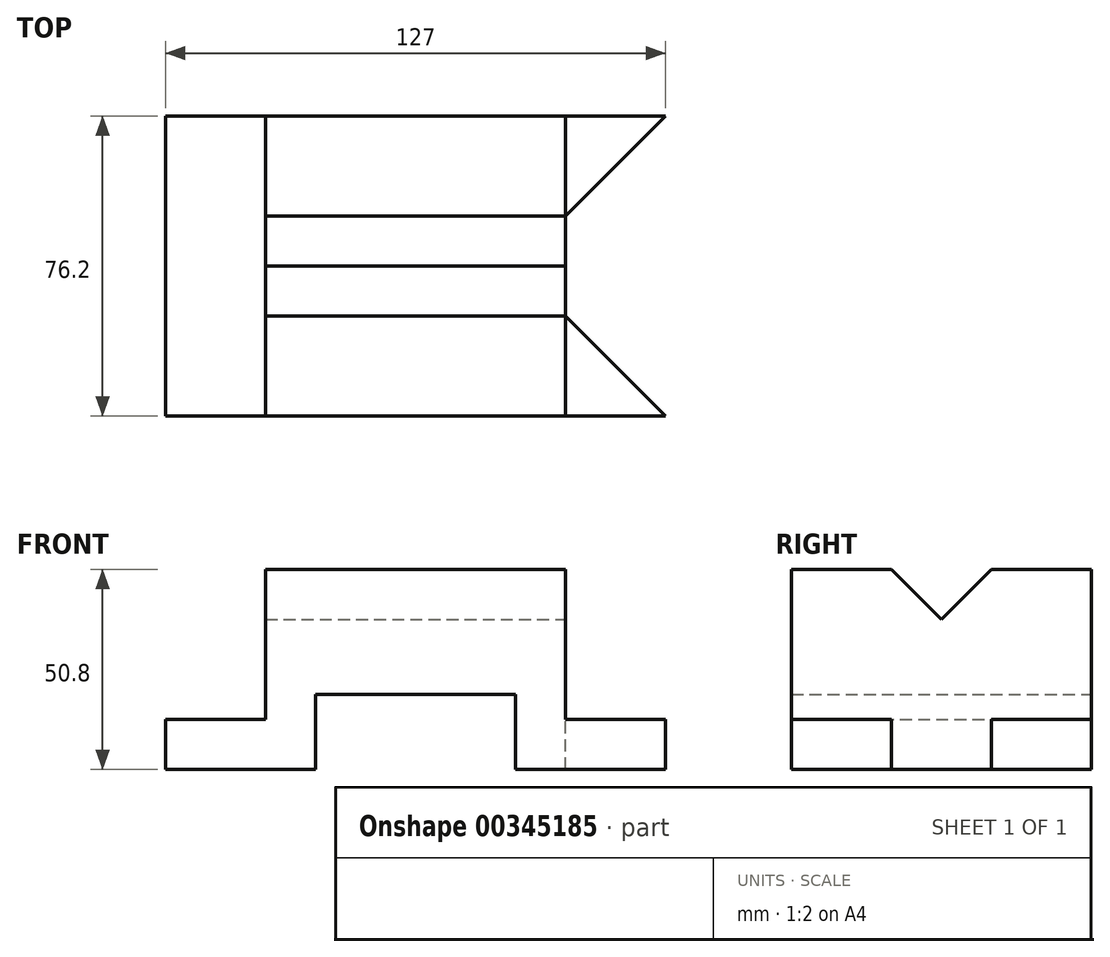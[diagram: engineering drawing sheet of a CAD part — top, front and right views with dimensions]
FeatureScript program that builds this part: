
annotation { "Feature Type Name" : "Feature", "Feature Type Description" : "" }
export const myFeature = defineFeature(function(context is Context, id is Id, definition is map)
    precondition{}
    {
        {
            var Q0;
            Q0=qCreatedBy(makeId("Front.planeOp"),FACE);
            var sketch = newSketch(context, id + "F0", { "sketchPlane" : qUnion([Q0])});
            skLineSegment(sketch, "E0", {"start": v(0, 0) * mm, "end": v(0, 12.7) * mm});
            skLineSegment(sketch, "E1", {"start": v(0, 12.7) * mm, "end": v(25.4, 12.7) * mm});
            skLineSegment(sketch, "E2", {"start": v(25.4, 12.7) * mm, "end": v(25.4, 50.8) * mm});
            skLineSegment(sketch, "E3", {"start": v(25.4, 50.8) * mm, "end": v(101.6, 50.8) * mm});
            skLineSegment(sketch, "E4", {"start": v(101.6, 50.8) * mm, "end": v(101.6, 12.7) * mm});
            skLineSegment(sketch, "E5", {"start": v(101.6, 12.7) * mm, "end": v(127, 12.7) * mm});
            skLineSegment(sketch, "E6", {"start": v(127, 12.7) * mm, "end": v(127, 0) * mm});
            skLineSegment(sketch, "E7", {"start": v(127, 0) * mm, "end": v(88.9, 0) * mm});
            skLineSegment(sketch, "E8", {"start": v(88.9, 0) * mm, "end": v(88.9, 19.05) * mm});
            skLineSegment(sketch, "E9", {"start": v(88.9, 19.05) * mm, "end": v(38.1, 19.05) * mm});
            skLineSegment(sketch, "E10", {"start": v(38.1, 19.05) * mm, "end": v(38.1, 0) * mm});
            skLineSegment(sketch, "E11", {"start": v(38.1, 0) * mm, "end": v(0, 0) * mm});
            skSolve(sketch);
        }
        {
            var Q0;
            Q0=makeQuery(id+"F0.imprint","IMPRINT",FACE,{"disambiguationData":[TD([[makeQuery(id+"F0.imprint","IMPRINT",EDGE,{"derivedFrom":sQuery(id+"F0.wireOp",EDGE,"E0")}),-1.0]])]});
            extrude(context, id + "F1", {"entities" : qUnion([Q0]), "depth" : 76.2 * mm});
        }
        {
            var Q0;
            Q0=makeQuery(id+"F1.opExtrude","SWEPT_FACE",FACE,{"disambiguationData":[OSD([sQuery(id+"F0.wireOp",EDGE,"E5")])]});
            var sketch = newSketch(context, id + "F2", { "sketchPlane" : qUnion([Q0])});
            skLineSegment(sketch, "E12", {"start": v(127, -76.2) * mm, "end": v(101.6, -50.8) * mm});
            skLineSegment(sketch, "E13", {"start": v(101.6, -50.8) * mm, "end": v(101.6, -25.4) * mm});
            skLineSegment(sketch, "E14", {"start": v(101.6, -25.4) * mm, "end": v(127, 0) * mm});
            skLineSegment(sketch, "E15", {"start": v(127, 0) * mm, "end": v(127, -76.2) * mm});
            skSolve(sketch);
        }
        {
            var Q0;
            Q0 = qSketchRegion(id + "F2", true);
            extrude(context, id + "F3", {"entities" : qUnion([Q0]), "operationType" : NewBodyOperationType.REMOVE, "endBound" : BoundingType.THROUGH_ALL, "oppositeDirection" : true, "depth" : 25.4 * mm});
        }
        {
            var Q0;
            Q0=makeQuery(id+"F3.boolean.opBoolean","MERGE",FACE,{"derivedFrom":[makeQuery(id+"F1.opExtrude","SWEPT_FACE",FACE,{"disambiguationData":[OSD([sQuery(id+"F0.wireOp",EDGE,"E4")])]}),makeQuery(id+"F3.opExtrude","SWEPT_FACE",FACE,{"disambiguationData":[OSD([sQuery(id+"F2.wireOp",EDGE,"E13")])]})]});
            var sketch = newSketch(context, id + "F4", { "sketchPlane" : qUnion([Q0])});
            skLineSegment(sketch, "E16", {"start": v(-50.8, 50.8) * mm, "end": v(-38.1, 38.1) * mm});
            skLineSegment(sketch, "E17", {"start": v(-38.1, 38.1) * mm, "end": v(-25.4, 50.8) * mm});
            skLineSegment(sketch, "E18", {"start": v(-25.4, 50.8) * mm, "end": v(-50.8, 50.8) * mm});
            skSolve(sketch);
        }
        {
            var Q0;
            Q0 = qSketchRegion(id + "F4", true);
            extrude(context, id + "F5", {"entities" : qUnion([Q0]), "operationType" : NewBodyOperationType.REMOVE, "endBound" : BoundingType.THROUGH_ALL, "oppositeDirection" : true, "depth" : 25.4 * mm});
        }
    });
